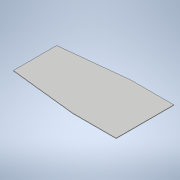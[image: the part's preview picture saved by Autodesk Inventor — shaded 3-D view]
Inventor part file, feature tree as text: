
AUTODESK INVENTOR PART (.ipt)
format: ipt  version: 2021 (Build 250183000, 183)  size: 95,744 bytes
history: native  units: in
note: dims shown in document units (in); Inventor stores cm internally (conversion verified against a paired STEP export)
features: extrude x1, sketch x1
ambient origin geometry x8: Origin, YZ Plane, XZ Plane, XY Plane, X Axis, Y Axis, Z Axis, Center Point
bodies: Solid1 (feature_tree)
feature tree (2):
  extrude  "Extrusion1"  Depth=0.125in
  sketch  "Sketch1"  dims[d0=8.0in d1=12.0in d2=30.5in d3=8.0in d4=12.0in d5=6.0in d6=6.0in d7=0.125in d8=0.0in]
